# Revit family: Kimberly Clark Economy Floor Stand SA408591 DWG
name_source: partatom
category: Generic Models
revit_build: Autodesk Revit 2018 (Build: 20170223_1515(x64)
units: mm (PartAtom-declared; Revit-internal decimal feet)

## family parameters
Always vertical = Yes
Can host rebar = No
Cut with Voids When Loaded = No
Part Type = Normal
Room Calculation Point = No
Round Connector Dimension = Use Diameter
Shared = No
Work Plane-Based = No

## types (1)
- Kimberly Clark Economy Floor Stand SA408591
    Bend Angle = 0 mm  [stored 0 ft]
    Height = 825 mm  [stored 2.70669 ft]
    Length = 325 mm  [stored 1.06627 ft]
    Manufacturer = Kimberly Clark
    Material = Steel
    Model = Economy Floor Stand SA408591
    URL = www.kcprofessional.com
    Width = 374 mm  [stored 1.22703 ft]

note: [stored X ft] marks values corroborated as IEEE doubles in the binary element streams (Revit-internal decimal feet)

## geometry (parser evidence)
native form markers: Sweep x2
no freeform markers — native parametric forms only
